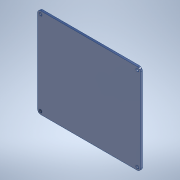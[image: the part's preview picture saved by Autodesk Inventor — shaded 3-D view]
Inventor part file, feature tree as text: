
AUTODESK INVENTOR PART (.ipt)
format: ipt  version: 2020 (Build 240168000, 168)  size: 128,000 bytes
history: native  units: mm
features: other x3, extrude x2, sketch x2, plane x1, reference x1, projected_geometry x1
ambient origin geometry x8: Origin, YZ Plane, XZ Plane, XY Plane, X Axis, Y Axis, Z Axis, Center Point
bodies: 实体1 (feature_tree)
feature tree (10):
  plane  "工作平面1"
  extrude  "拉伸1"  Depth=4.0mm
  extrude  "拉伸2"  Depth=4.0mm
  sketch  "草图1"  dims[d0=4.0mm d1=0.0mm d2=0.5mm]
  reference  "参考1"
  sketch  "草图2"  dims[d3=0.5mm d4=0.5mm d5=0.5mm d6=4.0mm d7=0.0mm]
  projected_geometry  "投影回路1"
  other  "<userpath>\Desktop\ME_course_project\课设试试\shaft_try_1.iam"
  other  "shaft_try_1.iam"
  other  "shang(1):1"
